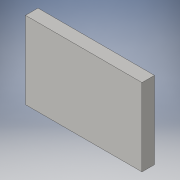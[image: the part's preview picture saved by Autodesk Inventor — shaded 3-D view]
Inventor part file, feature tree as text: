
AUTODESK INVENTOR PART (.ipt)
format: ipt  version: 2016 (Build 200138000, 138)  size: 84,992 bytes
history: native  units: in
note: dims shown in document units (in); Inventor stores cm internally (conversion verified against a paired STEP export)
features: extrude x1, sketch x1
ambient origin geometry x8: Origin, YZ Plane, XZ Plane, XY Plane, X Axis, Y Axis, Z Axis, Center Point
bodies: Solid1 (feature_tree)
feature tree (2):
  extrude  "Extrusion1"  Depth=0.344in TaperAngle=0.0deg
  sketch  "Sketch1"  dims[d0=1.6035in d1=1.6035in d2=0.344in d3=0.0in]
